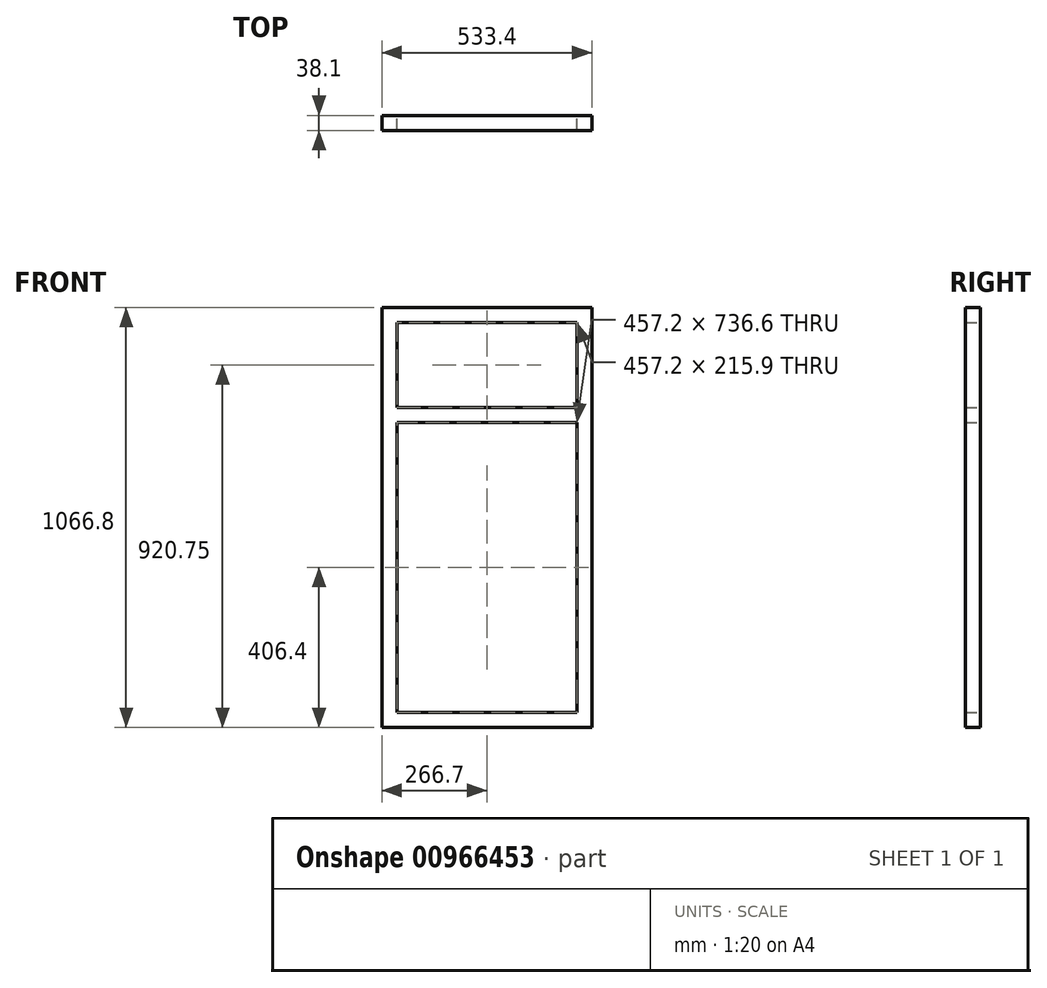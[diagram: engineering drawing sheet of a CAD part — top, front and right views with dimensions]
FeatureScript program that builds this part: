
annotation { "Feature Type Name" : "Feature", "Feature Type Description" : "" }
export const myFeature = defineFeature(function(context is Context, id is Id, definition is map)
    precondition{}
    {
        {
            var Q0;
            Q0=qCreatedBy(makeId("Front.planeOp"),FACE);
            var sketch = newSketch(context, id + "F0", { "sketchPlane" : qUnion([Q0])});
            skLineSegment(sketch, "E0.bottom", {"start": v(0, 0) * mm, "end": v(533.4, 0) * mm});
            skLineSegment(sketch, "E0.top", {"start": v(0, -1066.8) * mm, "end": v(533.4, -1066.8) * mm});
            skLineSegment(sketch, "E0.left", {"start": v(0, 0) * mm, "end": v(0, -1066.8) * mm});
            skLineSegment(sketch, "E0.right", {"start": v(533.4, 0) * mm, "end": v(533.4, -1066.8) * mm});
            skLineSegment(sketch, "E1.bottom", {"start": v(38.1, -38.1) * mm, "end": v(495.3, -38.1) * mm});
            skLineSegment(sketch, "E1.top", {"start": v(38.1, -1028.7) * mm, "end": v(495.3, -1028.7) * mm});
            skLineSegment(sketch, "E1.left", {"start": v(38.1, -38.1) * mm, "end": v(38.1, -1028.7) * mm});
            skLineSegment(sketch, "E1.right", {"start": v(495.3, -38.1) * mm, "end": v(495.3, -1028.7) * mm});
            skLineSegment(sketch, "E2", {"start": v(38.1, -533.4) * mm, "end": v(495.3, -533.4) * mm, "construction": true});
            skPoint(sketch, "E2.endSnap0", {"position": v(38.1, -533.4) * mm});
            skLineSegment(sketch, "E3.bottom", {"start": v(38.1, -254) * mm, "end": v(495.3, -254) * mm});
            skLineSegment(sketch, "E3.top", {"start": v(38.1, -292.1) * mm, "end": v(495.3, -292.1) * mm});
            skLineSegment(sketch, "E3.left", {"start": v(38.1, -254) * mm, "end": v(38.1, -292.1) * mm});
            skLineSegment(sketch, "E3.right", {"start": v(495.3, -254) * mm, "end": v(495.3, -292.1) * mm});
            skLineSegment(sketch, "E4", {"start": v(39.45, -20.64) * mm, "end": v(367.82, -20.64) * mm, "construction": true});
            skSolve(sketch);
        }
        {
            var Q0;
            Q0=makeQuery(id+"F0.imprint","IMPRINT",FACE,{"disambiguationData":[TD([[makeQuery(id+"F0.imprint","IMPRINT",EDGE,{"derivedFrom":sQuery(id+"F0.wireOp",EDGE,"E0.bottom")}),-1.0]])]});
            var Q1;
            {var subQ2=sQuery(id+"F0.wireOp",EDGE,"E3.bottom");Q1=makeQuery(id+"F0.imprint","IMPRINT",FACE,{"disambiguationData":[TD([[makeQuery(id+"F0.imprint","IMPRINT",EDGE,{"derivedFrom":subQ2}),-1.0]])]});}
            extrude(context, id + "F1", {"entities" : qUnion([Q0, Q1]), "depth" : 38.1 * mm, "offsetDistance" : 25.4 * mm});
        }
    });
